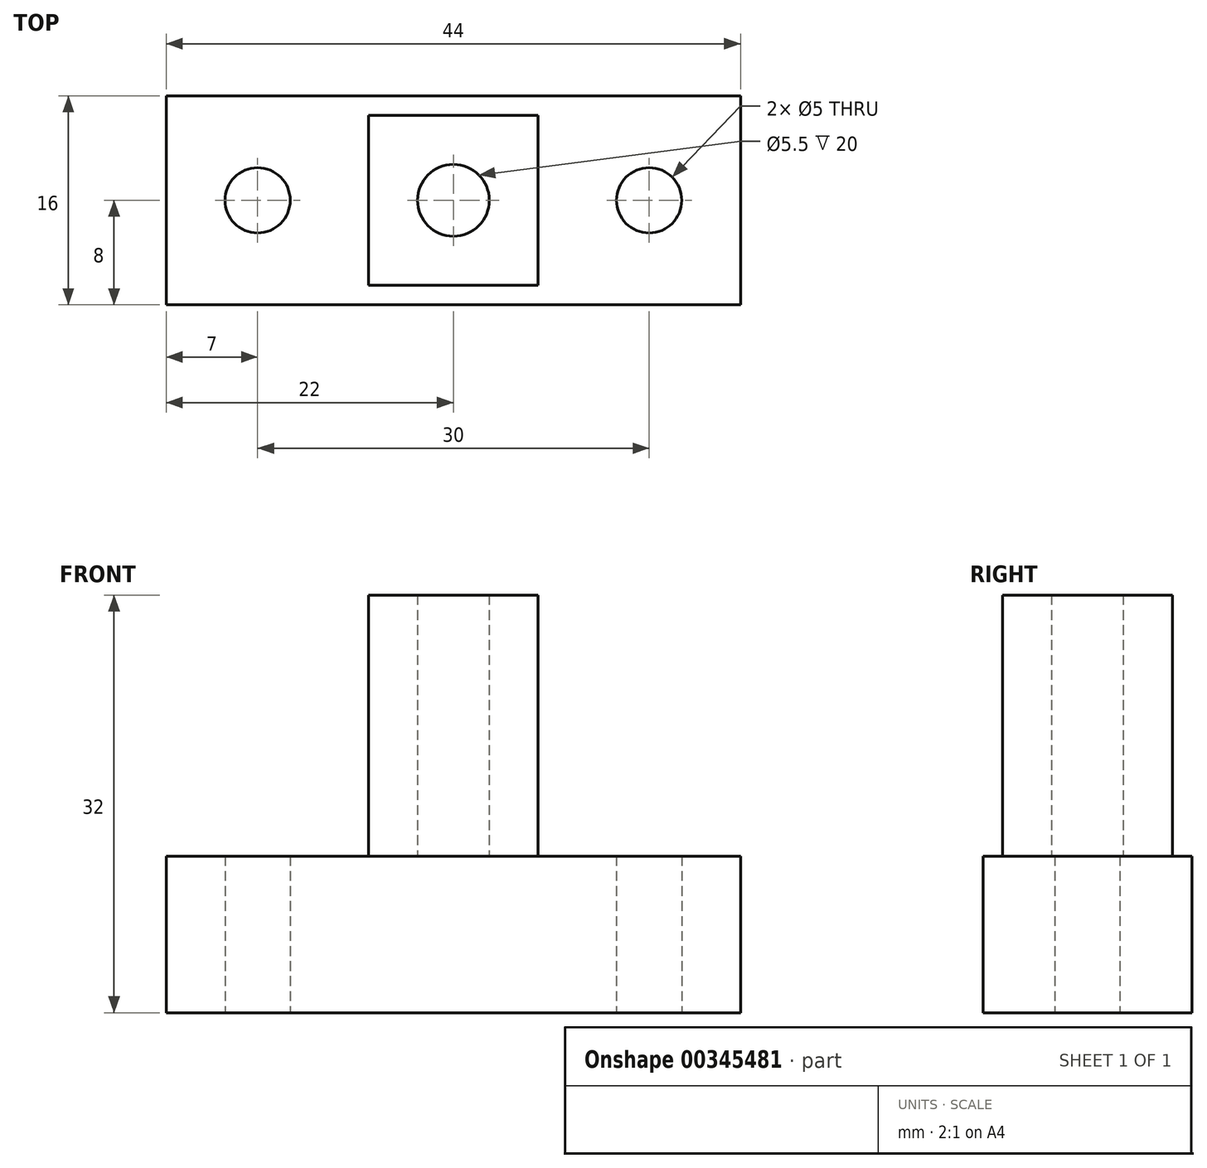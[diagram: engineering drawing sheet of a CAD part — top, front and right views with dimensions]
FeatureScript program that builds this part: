
annotation { "Feature Type Name" : "Feature", "Feature Type Description" : "" }
export const myFeature = defineFeature(function(context is Context, id is Id, definition is map)
    precondition{}
    {
        {
            var Q0;
            Q0=qCreatedBy(makeId("Top.planeOp"),FACE);
            var sketch = newSketch(context, id + "F0", { "sketchPlane" : qUnion([Q0])});
            skLineSegment(sketch, "E0.bottom", {"start": v(22, -8) * mm, "end": v(-22, -8) * mm});
            skLineSegment(sketch, "E0.top", {"start": v(22, 8) * mm, "end": v(-22, 8) * mm});
            skLineSegment(sketch, "E0.left", {"start": v(22, -8) * mm, "end": v(22, 8) * mm});
            skLineSegment(sketch, "E0.right", {"start": v(-22, -8) * mm, "end": v(-22, 8) * mm});
            skPoint(sketch, "E0.middle", {"position": v(0, 0) * mm});
            skCircle(sketch, "E1", {"center": v(-15, 0) * mm, "radius": 2.5 * mm});
            skCircle(sketch, "E2.MirrorC", {"center": v(15, 0) * mm, "radius": 2.5 * mm});
            skSolve(sketch);
        }
        {
            var Q0;
            Q0=makeQuery(id+"F0.imprint","IMPRINT",FACE,{"disambiguationData":[TD([[makeQuery(id+"F0.imprint","IMPRINT",EDGE,{"derivedFrom":sQuery(id+"F0.wireOp",EDGE,"E0.bottom")}),-1.0]])]});
            extrude(context, id + "F1", {"entities" : qUnion([Q0]), "depth" : 12 * mm});
        }
        {
            var Q0;
            Q0=makeQuery(id+"F1.opExtrude","CAP_FACE",FACE,{"disambiguationData":[OSD([sQuery(id+"F0.wireOp",EDGE,"E0.bottom"),sQuery(id+"F0.wireOp",EDGE,"E0.top"),sQuery(id+"F0.wireOp",EDGE,"E0.left"),sQuery(id+"F0.wireOp",EDGE,"E0.right"),sQuery(id+"F0.wireOp",EDGE,"E1"),sQuery(id+"F0.wireOp",EDGE,"E2.MirrorC")])],"isStart":false});
            var sketch = newSketch(context, id + "F2", { "sketchPlane" : qUnion([Q0])});
            skLineSegment(sketch, "E3.bottom", {"start": v(6.5, -6.5) * mm, "end": v(-6.5, -6.5) * mm});
            skLineSegment(sketch, "E3.top", {"start": v(6.5, 6.5) * mm, "end": v(-6.5, 6.5) * mm});
            skLineSegment(sketch, "E3.left", {"start": v(6.5, -6.5) * mm, "end": v(6.5, 6.5) * mm});
            skLineSegment(sketch, "E3.right", {"start": v(-6.5, -6.5) * mm, "end": v(-6.5, 6.5) * mm});
            skPoint(sketch, "E3.middle", {"position": v(0, 0) * mm});
            skCircle(sketch, "E4", {"center": v(0, 0) * mm, "radius": 2.75 * mm});
            skSolve(sketch);
        }
        {
            var Q0;
            Q0=makeQuery(id+"F2.imprint","IMPRINT",FACE,{"disambiguationData":[TD([[makeQuery(id+"F2.imprint","IMPRINT",EDGE,{"derivedFrom":sQuery(id+"F2.wireOp",EDGE,"E3.bottom")}),-1.0]])]});
            extrude(context, id + "F3", {"entities" : qUnion([Q0]), "operationType" : NewBodyOperationType.ADD, "depth" : 20 * mm});
        }
    });
